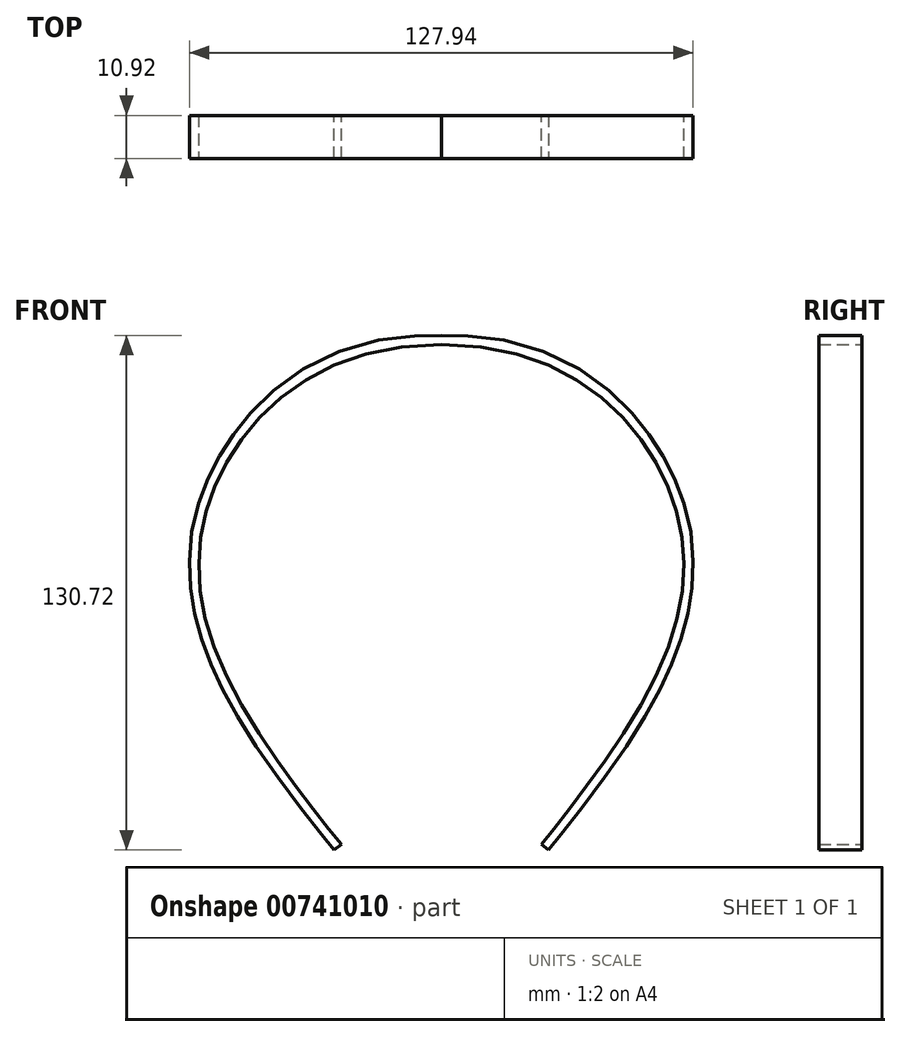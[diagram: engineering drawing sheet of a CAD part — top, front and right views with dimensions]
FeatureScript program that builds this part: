
annotation { "Feature Type Name" : "Feature", "Feature Type Description" : "" }
export const myFeature = defineFeature(function(context is Context, id is Id, definition is map)
    precondition{}
    {
        {
            var Q0;
            Q0=qCreatedBy(makeId("Front.planeOp"),FACE);
            var sketch = newSketch(context, id + "F0", { "sketchPlane" : qUnion([Q0])});
            skLineSegment(sketch, "E0", {"start": v(0, 0) * mm, "end": v(0, -127) * mm, "construction": true});
            skFitSpline(sketch, "E1", {"points": [v(0, 0) * mm, v(-54.96, -30.73) * mm, v(-57.24, -78.07) * mm, v(-25.4, -127) * mm], "startDerivative": vector(-242.27, 0) * mm, "endDerivative": vector(63.02, -80.06) * mm});
            skLineSegment(sketch, "E2", {"start": v(-25.4, -127) * mm, "end": v(-27.2, -128.4) * mm});
            skFitSpline(sketch, "E3.MirrorCS", {"points": [v(0, 0) * mm, v(54.96, -30.73) * mm, v(57.24, -78.07) * mm, v(25.4, -127) * mm], "startDerivative": vector(242.27, 0) * mm, "endDerivative": vector(-63.02, -80.06) * mm});
            skFitSpline(sketch, "E4.0", {"points": [v(0, 2.29) * mm, v(-5.18, 2.29) * mm, v(-14.87, 1.37) * mm, v(-27.44, -2.39) * mm, v(-38.07, -8.1) * mm, v(-45.34, -14.16) * mm, v(-50.25, -19.55) * mm, v(-53.48, -23.8) * mm, v(-56.27, -28.24) * mm, v(-58.64, -32.8) * mm, v(-60.6, -37.45) * mm, v(-62.62, -43.82) * mm, v(-63.76, -50.4) * mm, v(-63.95, -57.17) * mm, v(-63.62, -62.33) * mm, v(-62.8, -67.57) * mm, v(-61.5, -72.88) * mm, v(-59.7, -78.27) * mm, v(-57.38, -83.72) * mm, v(-54.67, -89.16) * mm, v(-50.62, -96.34) * mm, v(-45, -105.03) * mm, v(-38.11, -114.53) * mm, v(-31.81, -122.63) * mm, v(-28.5, -126.76) * mm, v(-27.2, -128.41) * mm]});
            skFitSpline(sketch, "E4.1", {"points": [v(0, 2.29) * mm, v(5.18, 2.29) * mm, v(14.87, 1.37) * mm, v(27.44, -2.39) * mm, v(38.07, -8.1) * mm, v(45.34, -14.16) * mm, v(50.25, -19.55) * mm, v(53.48, -23.8) * mm, v(56.27, -28.24) * mm, v(58.64, -32.8) * mm, v(60.6, -37.45) * mm, v(62.62, -43.82) * mm, v(63.76, -50.4) * mm, v(63.95, -57.17) * mm, v(63.62, -62.33) * mm, v(62.8, -67.57) * mm, v(61.5, -72.88) * mm, v(59.7, -78.27) * mm, v(57.38, -83.72) * mm, v(54.67, -89.16) * mm, v(50.62, -96.34) * mm, v(45, -105.03) * mm, v(38.11, -114.53) * mm, v(31.81, -122.63) * mm, v(28.5, -126.76) * mm, v(27.2, -128.41) * mm]});
            skLineSegment(sketch, "E5", {"start": v(25.4, -127) * mm, "end": v(27.2, -128.4) * mm});
            skSolve(sketch);
        }
        {
            var Q0;
            Q0 = qSketchRegion(id + "F0", true);
            extrude(context, id + "F1", {"entities" : qUnion([Q0]), "endBound" : BoundingType.SYMMETRIC, "depth" : 10.92 * mm, "offsetDistance" : 25 * mm});
        }
    });
